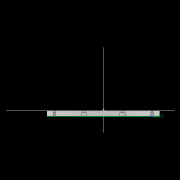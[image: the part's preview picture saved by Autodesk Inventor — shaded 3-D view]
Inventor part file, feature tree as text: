
AUTODESK INVENTOR PART (.ipt)
format: ipt  version: 2022.2 (Build 262287010, 287A)  size: 694,272 bytes
history: native  units: mm
features: extrude x19, sketch x18, pattern_circular x15, other x14, revolve x7, hole x7, move_body x4, fillet x2, draft x2
ambient origin geometry x8: Origin, YZ Plane, XZ Plane, XY Plane, X Axis, Y Axis, Z Axis, Center Point
bodies: Solid1 (feature_tree), Solid2 (feature_tree), Solid3 (feature_tree), Solid4 (feature_tree), Solid5 (feature_tree)
feature tree (88):
  sketch  "Sketch7"  dims[d21=0.5mm]
  other  "Roller1"
  other  "Roller2"
  sketch  "Sketch22"  dims[d39=0.05mm]
  sketch  "Sketch2"  dims[d17=0.05mm]
  sketch  "Sketch23"  dims[d41=0.05mm]
  other  "RevRoller1"
  fillet  "Fillet1"  Radius=0.05mm
  pattern_circular  "Circular Pattern13"  Count=6  [1 undecoded]
  move_body  "Move Body7"
  revolve  "Revolution13"  Angle=30.0deg
  fillet  "Fillet3"  [1 undecoded]
  pattern_circular  "Circular Pattern14"  [2 undecoded]
  move_body  "Move Body6"
  revolve  "Revolution14"  [1 undecoded]
  other  "OuterRim_Top2"
  other  "OuterRim_Bottom2"
  extrude  "Extrusion9"  TaperAngle=90.0deg  [1 undecoded]
  sketch  "Sketch24"  dims[d42=0.5mm]
  extrude  "Extrusion10"  Depth=3.0mm
  extrude  "Extrusion11"  Depth=3.0mm
  pattern_circular  "Circular Pattern15"  [2 undecoded]
  sketch  "Sketch25"  dims[d43=0.5mm]
  extrude  "Extrusion12"  Depth=3.0mm
  extrude  "Extrusion14"  Depth=3.0mm
  extrude  "Extrusion15"  Depth=3.0mm
  pattern_circular  "Circular Pattern16"  [2 undecoded]
  extrude  "Extrusion16"  Depth=3.0mm
  extrude  "Extrusion17"  Depth=3.0mm
  hole  "Hole9"  [1 undecoded]
  pattern_circular  "Circular Pattern17"  [2 undecoded]
  sketch  "Sketch27"  dims[d45=0.5mm]
  hole  "Hole10"  [1 undecoded]
  hole  "Hole11"  [1 undecoded]
  pattern_circular  "Circular Pattern18"  [2 undecoded]
  extrude  "Extrusion18"  Depth=3.0mm
  extrude  "Extrusion19"  Depth=3.0mm
  pattern_circular  "Circular Pattern19"  [2 undecoded]
  sketch  "Sketch28"  dims[d46=0.5mm d47=0.5mm d48=2.0mm d50=90.0deg d56=14.029612mm d57=4.025mm d90=16.473921mm d107=0.05mm d108=0.05mm d109=0.05mm d110=0.05mm d112=0.5mm d113=0.5mm d114=0.5mm d115=14.644822mm d116=14.607374mm d117=1.0mm d118=0.05mm d119=0.05mm d120=0.05mm d121=0.05mm d122=0.5mm d123=0.5mm d124=14.644822mm d125=14.607374mm d126=1.0mm d127=90.0deg d128=30.0deg d129=90.0deg d167=8.972256mm d173=10.814812mm d201=53.5mm d202=90.0deg d203=90.0deg d204=90.0deg d218=53.5mm d226=5.4mm d232=0.0mm d233=3600.0mm d234=10.502mm d235=0.0mm d243=1.902mm d244=0.0mm d246=2.75mm d247=5.251mm d248=0.0mm d249=3.0mm d250=0.0mm d251=90.0mm d252=360.0deg d254=2.75mm d255=3.0mm d256=5.251mm d257=0.0mm d258=3.0mm d259=0.0mm d260=90.0mm d261=360.0deg d277=76.5mm d281=73.5mm d282=24.65mm d283=6.0mm d284=4.0mm d285=2.0mm d286=90.0deg d287=5.251mm d288=0.0mm d289=60.0mm d290=360.0deg d292=0.436332mm d293=60.0mm d294=90.0mm d295=3.0mm d296=6.0mm d297=5.5mm d298=3.0mm d299=90.0deg d300=5.251mm d301=0.0mm d302=60.0mm d303=360.0deg d305=30.0deg d306=73.5mm d307=24.65mm d308=6.0mm d309=5.5mm d310=3.0mm d311=90.0deg d312=5.251mm d313=0.0mm d314=60.0mm d315=360.0deg d317=90.0mm d318=60.0mm d319=30.0deg d320=5.4mm d321=5.4mm d322=3.0mm d323=6.0mm d324=5.5mm d325=3.0mm d326=90.0deg d327=5.251mm d328=0.0mm d329=2.4mm d330=0.0mm d331=60.0mm d332=360.0deg d343=17.307186mm d344=17.309884mm d345=0.025mm d346=0.025mm d347=0.1mm d348=0.1mm d349=17.309884mm d350=17.307186mm d351=0.025mm d352=0.025mm d354=0.1mm d355=17.307186mm d356=17.309884mm d357=1.0mm d358=90.0deg d359=0.5mm d360=60.0mm d361=360.0deg d363=30.0deg d367=8.1mm d369=4.014775mm d370=0.1mm d371=1.0mm d372=30.0deg d373=90.0deg d374=0.5mm d375=60.0mm d376=360.0deg d378=90.0deg d379=0.1mm d380=0.1mm d381=0.1mm d382=0.1mm d383=0.1mm d384=10.502mm d385=0.0mm d386=0.0mm d391=1.0mm d392=53.5mm d393=1.5mm d394=1.5mm d395=1.5mm d396=1.5mm d397=90.0deg d398=90.0deg d399=90.0deg d400=53.5mm d401=10.502mm d402=0.0mm d403=2.75mm d404=1.5mm d405=10.502mm d406=0.0mm d407=3.0mm d408=0.0mm d409=90.0mm d410=360.0deg d412=5.4mm d413=5.251mm d414=0.0mm d417=5.4mm d418=2.4mm d419=0.0mm d420=2.4mm d421=0.0mm d422=90.0mm d423=360.0deg d425=60.0mm d426=90.0mm d427=1.5mm d428=1.5mm d429=5.4mm d430=5.4mm d431=5.251mm d432=0.0mm d433=2.4mm d434=0.0mm d435=30.0deg d436=73.5mm d437=24.65mm d438=6.0mm d439=4.0mm d440=2.0mm d441=90.0deg d442=5.251mm d443=0.0mm d444=60.0mm d445=360.0deg d447=3.0mm d448=6.0mm d449=5.5mm d450=3.0mm d451=90.0deg d452=5.251mm d453=0.0mm d454=24.65mm d455=6.0mm d456=5.5mm d457=3.0mm d458=90.0deg d459=5.251mm d460=0.0mm d461=60.0mm d462=360.0deg d464=5.251mm d465=0.0mm d466=3.0mm d467=0.0mm d468=90.0mm d469=360.0deg d472=1.5mm d474=5.251mm d475=0.0mm d481=3.0mm d482=0.0mm d483=90.0mm d484=360.0deg d486=0.436332mm d49=0.872665mm d51=0.872665mm d52=0.872665mm d236=0.5mm d237=0.872665mm d238=0.5mm d239=0.872665mm d291=0.0625mm d415=0.5mm d416=0.872665mm d471=0.5mm d473=0.5mm]
  extrude  "Extrusion20"  Depth=3.0mm
  extrude  "Extrusion22"  Depth=3.0mm
  pattern_circular  "Circular Pattern21"  [2 undecoded]
  draft  "FaceDraft2"
  other  "InnerRim"
  other  "OuterRim_Top"
  other  "OuterRim_Bottom"
  extrude  "Extrusion2"  Depth=3.0mm
  sketch  "Sketch13"  dims[d24=0.5mm]
  extrude  "Extrusion3"  Depth=3.0mm
  sketch  "Sketch15"  dims[d29=360.0deg d30=60.0mm]
  extrude  "Extrusion4"  TaperAngle=90.0deg  [1 undecoded]
  extrude  "Extrusion5"  TaperAngle=30.0deg  [1 undecoded]
  pattern_circular  "Circular Pattern6"  Angle=90.0deg  [1 undecoded]
  sketch  "Sketch16"  dims[d31=360.0deg d35=30.0deg d36=90.0deg]
  extrude  "Extrusion6"  Depth=3.0mm
  extrude  "Extrusion7"  Depth=3.0mm
  pattern_circular  "Circular Pattern7"  [2 undecoded]
  hole  "Hole5"  [1 undecoded]
  pattern_circular  "Circular Pattern9"  Angle=90.0deg  [1 undecoded]
  draft  "FaceDraft1"
  hole  "Hole6"  [1 undecoded]
  pattern_circular  "Circular Pattern10"  [2 undecoded]
  hole  "Hole7"  [1 undecoded]
  pattern_circular  "Circular Pattern11"  Count=360  [1 undecoded]
  hole  "Hole8"  [1 undecoded]
  extrude  "Extrusion8"  TaperAngle=0.0deg  [1 undecoded]
  pattern_circular  "Circular Pattern12"  [2 undecoded]
  sketch  "Sketch8"  dims[d22=0.5mm]
  sketch  "Sketch9"  dims[d23=0.5mm]
  revolve  "Revolution4"  [1 undecoded]
  move_body  "Move Body4"
  revolve  "Revolution5"  [1 undecoded]
  sketch  "Sketch5"  dims[d19=0.5mm]
  sketch  "Sketch6"  dims[d20=0.5mm]
  revolve  "Revolution3"  [1 undecoded]
  sketch  "Sketch4"  dims[d18=0.05mm]
  revolve  "Revolution1"  [1 undecoded]
  pattern_circular  "Circular Pattern1"  [2 undecoded]
  move_body  "Move Body3"
  revolve  "Revolution2"  [1 undecoded]
  other  "2D Equation Curve1"
  sketch  "Sketch14"  dims[d28=2.0mm]
  other  "Work Axis1"
  other  "Work Axis2"
  other  "Work Axis3"
  other  "Work Axis4"
  other  "Work Axis5"
  sketch  "Sketch26"  dims[d44=0.5mm]
note: 44 required parameter values undecoded (feature->parameter linkage not recoverable at this tier; creation-order binding heuristic only, values carry confidence <= 0.55)